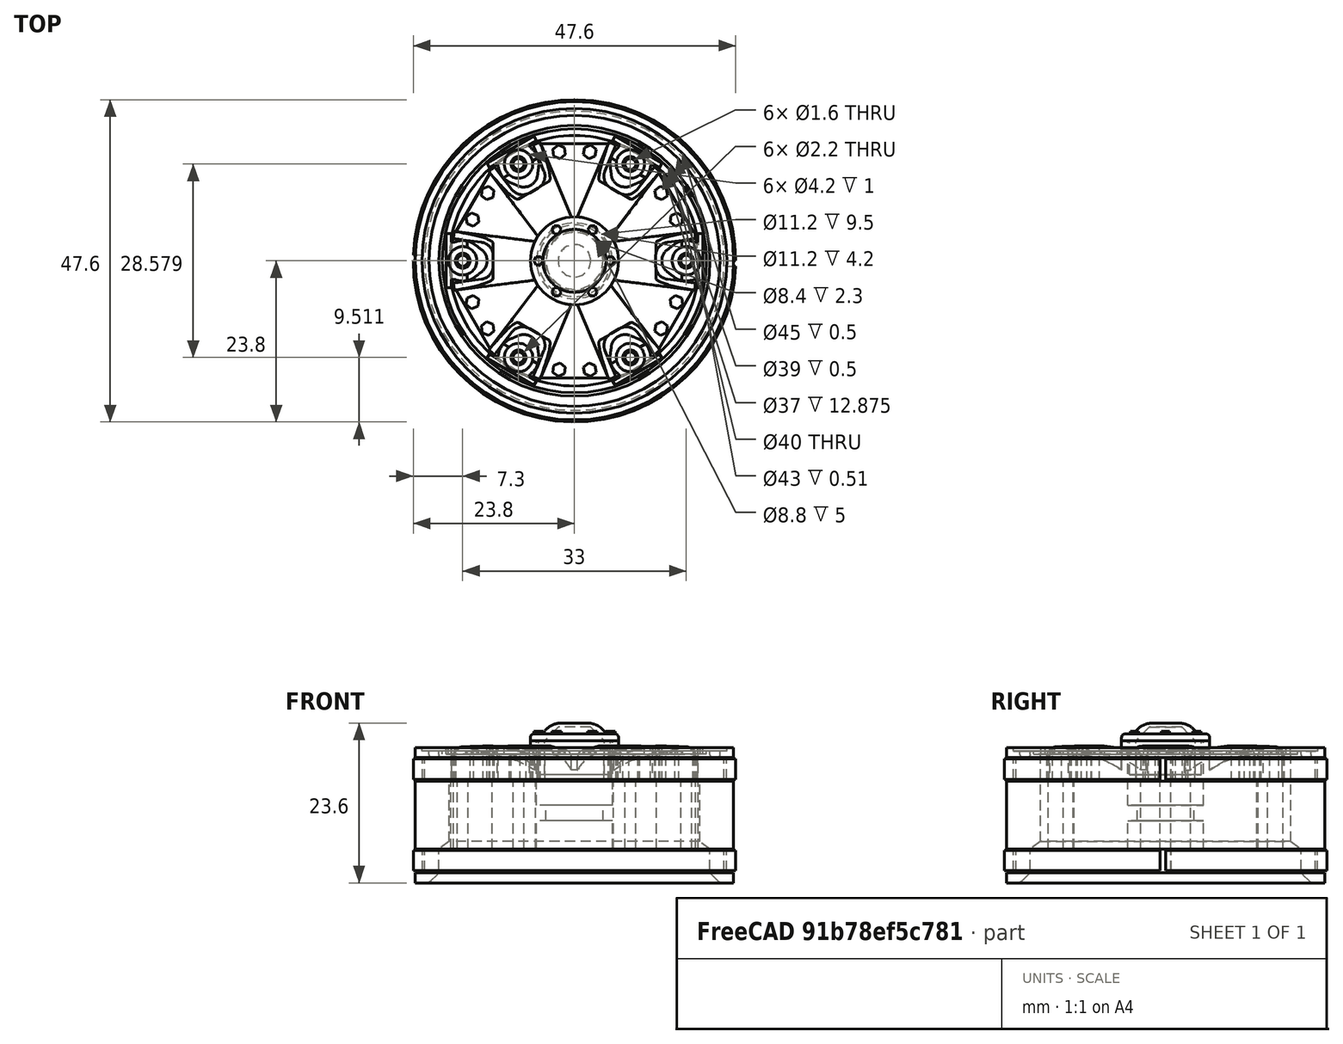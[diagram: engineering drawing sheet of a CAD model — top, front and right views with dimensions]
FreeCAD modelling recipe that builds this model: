
FCSTD DOCUMENT  (FreeCAD 0.18.4R)
Label: trilex_middle
License: All rights reserved
LicenseURL: http://en.wikipedia.org/wiki/All_rights_reserved
objects: Part::Cylinder×39, Part::MultiFuse×27, Part::Cut×26, Part::Feature×23, Part::Fillet×8, Part::Box×6, Part::Chamfer×6, Part::RegularPolygon×4, Part::Extrusion×4, Part::Cone×2
note: 145 computed .brp shape members not serialized (recipe doc carries the construction recipe); baked Part::Feature solids carry a one-line shape summary decoded from their .brp

FEATURE [Part::Cylinder] Cylinder
  Angle = 360
  AttacherType = Attacher::AttachEngine3D
  Height = 20
  Radius = 23.5
FEATURE [Part::RegularPolygon] RegularPolygon001  label="Regular polygon001"
  AttacherType = Attacher::AttachEngine3D
  Circumradius = 1
  Placement = pos=(16.25,0,18.5) rot=(0,0,1;0rad)
  Polygon = 6
FEATURE [Part::Extrusion] Extrude010
  Base = -> RegularPolygon001
  Dir = (0,0,1)
  DirMode = 0
  FaceMakerClass = Part::FaceMakerBullseye
  LengthFwd = 1
  LengthRev = 0
  Placement = pos=(0,0,0) rot=(0,0,1;0.383972rad)
  Solid = true
  Symmetric = false
FEATURE [Part::Feature] Fillet006004001  label="Fillet006008"
  Placement = pos=(0,0,0) rot=(0,0,1;1.0472rad)
  shape: bbox 9.68 x 11.05 x 7 mm, 10 faces (baked)
FEATURE [Part::Feature] Fillet006004005  label="Fillet006012"
  Placement = pos=(0,0,0) rot=(0,0,-1;1.0472rad)
  shape: bbox 9.68 x 11.05 x 7 mm, 10 faces (baked)
FEATURE [Part::Cylinder] Cylinder018
  Angle = 360
  AttacherType = Attacher::AttachEngine3D
  Height = 0.5
  Placement = pos=(0,0,19.5) rot=(0,0,1;0rad)
  Radius = 22.5
FEATURE [Part::Cylinder] Cylinder027
  Angle = 360
  AttacherType = Attacher::AttachEngine3D
  Height = 4
  Placement = pos=(0,0,3) rot=(0,0,1;0rad)
  Radius = 4.2
FEATURE [Part::Cylinder] Cylinder002
  Angle = 360
  AttacherType = Attacher::AttachEngine3D
  Height = 17
  Radius = 22.1
FEATURE [Part::Cylinder] Cylinder007
  Angle = 360
  AttacherType = Attacher::AttachEngine3D
  Height = 1
  Placement = pos=(0,0,19) rot=(0,0,1;0rad)
  Radius = 19.5
FEATURE [Part::Cylinder] Cylinder025
  Angle = 360
  AttacherType = Attacher::AttachEngine3D
  Height = 4.2
  Radius = 5.6
FEATURE [Part::Cylinder] Cylinder003
  Angle = 360
  AttacherType = Attacher::AttachEngine3D
  Height = 17
  Radius = 22
FEATURE [Part::Cylinder] Cylinder026
  Angle = 360
  AttacherType = Attacher::AttachEngine3D
  Height = 10
  Placement = pos=(0,0,6.5) rot=(0,0,1;0rad)
  Radius = 5.6
FEATURE [Part::Cylinder] Cylinder004
  Angle = 360
  AttacherType = Attacher::AttachEngine3D
  Height = 10
  Placement = pos=(0,0,0.5) rot=(0,0,1;0rad)
  Radius = 23.5
FEATURE [Part::Cylinder] Cylinder006
  Angle = 360
  AttacherType = Attacher::AttachEngine3D
  Height = 20
  Radius = 18.5
FEATURE [Part::Cylinder] Cylinder001
  Angle = 360
  AttacherType = Attacher::AttachEngine3D
  Height = 17
  Radius = 23.5
FEATURE [Part::Feature] Cut057003014003  label="Cut057003017"
  Placement = pos=(0,0,0) rot=(0,0,1;3.14159rad)
  shape: bbox 12.98 x 8.687 x 5.868 mm, 9 faces (baked)
FEATURE [Part::Feature] Extrude010001  label="Extrude011"
  Placement = pos=(0,0,0) rot=(0,0,1;0.663225rad)
  shape: bbox 1.854 x 1.981 x 1 mm, 8 faces (baked)
FEATURE [Part::MultiFuse] Fusion058
  Refine = true
  Shapes = -> [Extrude010001,Extrude010]
FEATURE [Part::Feature] Fusion058001  label="Fusion059"
  Placement = pos=(0,0,0) rot=(0,0,1;1.0472rad)
  shape: bbox 6.377 x 1.981 x 1 mm, 16 faces, 2 solids (baked)
FEATURE [Part::Feature] Fusion058005  label="Fusion063"
  Placement = pos=(0,0,0) rot=(0,0,-1;1.0472rad)
  shape: bbox 4.116 x 5.898 x 1 mm, 16 faces, 2 solids (baked)
FEATURE [Part::Feature] Fusion058004  label="Fusion062"
  Placement = pos=(0,0,0) rot=(0,0,1;4.18879rad)
  shape: bbox 6.377 x 1.981 x 1 mm, 16 faces, 2 solids (baked)
FEATURE [Part::Feature] Fillet006004003  label="Fillet006010"
  Placement = pos=(0,0,0) rot=(0,0,1;3.14159rad)
  shape: bbox 10 x 7 x 7 mm, 10 faces (baked)
FEATURE [Part::Feature] Fusion058002  label="Fusion060"
  Placement = pos=(0,0,0) rot=(0,0,1;2.0944rad)
  shape: bbox 4.116 x 5.898 x 1 mm, 16 faces, 2 solids (baked)
FEATURE [Part::Cut] Cut002
  Base = -> Cylinder004
  Placement = pos=(0,0,4.5) rot=(0,0,1;0rad)
  Refine = true
  Tool = -> Cylinder003
FEATURE [Part::Feature] Cut057003014004  label="Cut057003018"
  Placement = pos=(0,0,0) rot=(0,0,1;4.18879rad)
  shape: bbox 12.4 x 14.34 x 5.868 mm, 9 faces (baked)
FEATURE [Part::Cut] Cut
  Base = -> Cylinder001
  Placement = pos=(0,0,1.5) rot=(0,0,1;0rad)
  Refine = true
  Tool = -> Cylinder002
FEATURE [Part::Cut] Cut001
  Base = -> Cylinder
  Refine = true
  Tool = -> Cut
FEATURE [Part::MultiFuse] Fusion
  Refine = true
  Shapes = -> [Cut002,Cut001]
FEATURE [Part::MultiFuse] Fusion006
  Placement = pos=(0,0,5) rot=(0,0,1;0rad)
  Refine = true
  Shapes = -> [Cylinder025,Cylinder026,Cylinder027]
FEATURE [Part::Cylinder] Cylinder101
  Angle = 360
  AttacherType = Attacher::AttachEngine3D
  Height = 3.8
  Placement = pos=(0,0,19.4) rot=(0,0,1;0rad)
  Radius = 5
FEATURE [Part::Cylinder] Cylinder102
  Angle = 288
  AttacherType = Attacher::AttachEngine3D
  Height = 5
  Placement = pos=(16.5,0,15) rot=(0,0,1;0.628319rad)
  Radius = 3
FEATURE [Part::Box] Box012  label="Cube012"
  AttacherType = Attacher::AttachEngine3D
  Height = 5
  Length = 2
  Placement = pos=(16.5,-2.75,15) rot=(0,0,1;0rad)
  Width = 5.5
FEATURE [Part::Cylinder] Cylinder103
  Angle = 360
  AttacherType = Attacher::AttachEngine3D
  Height = 5
  Placement = pos=(15.5,0,15) rot=(0,0,1;0rad)
  Radius = 1.1
FEATURE [Part::Box] Box013  label="Cube013"
  AttacherType = Attacher::AttachEngine3D
  Height = 5
  Length = 0.75
  Placement = pos=(18.2,-4,15) rot=(0,0,1;0rad)
  Width = 8
FEATURE [Part::Cylinder] Cylinder104
  Angle = 360
  AttacherType = Attacher::AttachEngine3D
  Height = 1
  Placement = pos=(15.5,0,19) rot=(0,0,1;0rad)
  Radius = 2.1
FEATURE [Part::MultiFuse] Fusion044
  Refine = true
  Shapes = -> [Box012,Box013,Cylinder102]
FEATURE [Part::MultiFuse] Fusion045
  Placement = pos=(1,0,0) rot=(0,0,1;0rad)
  Refine = true
  Shapes = -> [Cylinder103,Cylinder104]
FEATURE [Part::Box] Box014  label="Cube014"
  AttacherType = Attacher::AttachEngine3D
  Height = 1
  Length = 7
  Placement = pos=(11.2,-4,18.75) rot=(0,-1,0;0.261799rad)
  Width = 8
FEATURE [Part::Cylinder] Cylinder105
  Angle = 360
  AttacherType = Attacher::AttachEngine3D
  Height = 5
  Placement = pos=(15,0,15) rot=(0,0,1;0rad)
  Radius = 2.1
FEATURE [Part::MultiFuse] Fusion046
  Refine = true
  Shapes = -> [Fusion044,Cylinder105]
FEATURE [Part::Feature] Cut057003001  label="Cut057005"
  Placement = pos=(0,0,0) rot=(0,0,1;1.0472rad)
  shape: bbox 7.689 x 7.521 x 5.306 mm, 18 faces (baked)
FEATURE [Part::Feature] Cut057003002  label="Cut057006"
  Placement = pos=(0,0,0) rot=(0,0,1;2.0944rad)
  shape: bbox 7.689 x 7.521 x 5.306 mm, 18 faces (baked)
FEATURE [Part::Feature] Cut057003003  label="Cut057007"
  Placement = pos=(0,0,0) rot=(0,0,1;3.14159rad)
  shape: bbox 6.05 x 8 x 5.306 mm, 18 faces (baked)
FEATURE [Part::Feature] Cut057003004  label="Cut057008"
  Placement = pos=(0,0,0) rot=(0,0,1;4.18879rad)
  shape: bbox 7.689 x 7.521 x 5.306 mm, 18 faces (baked)
FEATURE [Part::Feature] Cut057003005  label="Cut057009"
  Placement = pos=(0,0,0) rot=(0,0,-1;1.0472rad)
  shape: bbox 7.689 x 7.521 x 5.306 mm, 18 faces (baked)
FEATURE [Part::Cylinder] Cylinder126
  Angle = 360
  AttacherType = Attacher::AttachEngine3D
  Height = 2
  Placement = pos=(0,0,19) rot=(0,0,1;0rad)
  Radius = 21.5
FEATURE [Part::Cylinder] Cylinder127
  Angle = 360
  AttacherType = Attacher::AttachEngine3D
  Height = 2
  Placement = pos=(0,0,19) rot=(0,0,1;0rad)
  Radius = 20
FEATURE [Part::Cut] Cut061004
  Base = -> Cylinder126
  Placement = pos=(0,0,-0.5) rot=(0,0,1;0rad)
  Refine = true
  Tool = -> Cylinder127
FEATURE [Part::RegularPolygon] RegularPolygon  label="Regular polygon"
  AttacherType = Attacher::AttachEngine3D
  Circumradius = 20
  Polygon = 6
FEATURE [Part::Cylinder] Cylinder128
  Angle = 360
  AttacherType = Attacher::AttachEngine3D
  Height = 15
  Placement = pos=(0,0,5) rot=(0,0,1;0rad)
  Radius = 18.25
FEATURE [Part::Extrusion] Extrude009
  Base = -> RegularPolygon
  Dir = (0,0,-1)
  DirMode = 0
  FaceMakerClass = Part::FaceMakerBullseye
  LengthFwd = 14
  LengthRev = 0
  Placement = pos=(0,0,19) rot=(0,0,1;0rad)
  Solid = true
  Symmetric = false
FEATURE [Part::Cylinder] Cylinder129
  Angle = 360
  AttacherType = Attacher::AttachEngine3D
  Height = 15
  Placement = pos=(0,0,5) rot=(0,0,1;0rad)
  Radius = 25
FEATURE [Part::Cut] Cut057003007
  Base = -> Cylinder129
  Refine = true
  Tool = -> Cylinder128
FEATURE [Part::Cut] Cut057003008
  Base = -> Extrude009
  Refine = true
  Tool = -> Cut057003007
FEATURE [Part::Cylinder] Cylinder130
  Angle = 360
  AttacherType = Attacher::AttachEngine3D
  Height = 6
  Placement = pos=(0,0,15) rot=(0,0,1;0rad)
  Radius = 6.5
FEATURE [Part::Cylinder] Cylinder131
  Angle = 360
  AttacherType = Attacher::AttachEngine3D
  Height = 15
  Placement = pos=(-16.5,0,1) rot=(0,0,1;0rad)
  Radius = 0.8
FEATURE [Part::Cylinder] Cylinder132
  Angle = 360
  AttacherType = Attacher::AttachEngine3D
  Height = 15
  Placement = pos=(16.5,0,1) rot=(0,0,1;0rad)
  Radius = 0.8
FEATURE [Part::Cylinder] Cylinder133
  Angle = 360
  AttacherType = Attacher::AttachEngine3D
  Height = 15
  Placement = pos=(-16.5,0,1) rot=(0,0,1;0rad)
  Radius = 0.8
FEATURE [Part::MultiFuse] Fusion051
  Placement = pos=(0,0,0) rot=(0,0,1;1.0472rad)
  Refine = true
  Shapes = -> [Cylinder133,Cylinder132]
FEATURE [Part::Cylinder] Cylinder134
  Angle = 360
  AttacherType = Attacher::AttachEngine3D
  Height = 15
  Placement = pos=(-16.5,0,1) rot=(0,0,1;0rad)
  Radius = 0.8
FEATURE [Part::Cylinder] Cylinder135
  Angle = 360
  AttacherType = Attacher::AttachEngine3D
  Height = 15
  Placement = pos=(16.5,0,1) rot=(0,0,1;0rad)
  Radius = 0.8
FEATURE [Part::MultiFuse] Fusion052
  Placement = pos=(0,0,0) rot=(0,0,1;2.0944rad)
  Refine = true
  Shapes = -> [Cylinder134,Cylinder135]
FEATURE [Part::Box] Box015  label="Cube015"
  AttacherType = Attacher::AttachEngine3D
  Height = 6
  Length = 17
  Placement = pos=(5,-4.5,15) rot=(0,0,1;0rad)
  Width = 9
FEATURE [Part::Chamfer] Chamfer004
  Base = -> Box015
  Edges = 2 edges: [Edge1 r1=1.75 r2=14,Edge3 r1=1.75 r2=14]
FEATURE [Part::Chamfer] Chamfer005
  Base = -> Chamfer004
  Edges = 1 edges: [Edge1 r1=1.5 r2=14]
FEATURE [Part::Box] Box  label="Cube"
  AttacherType = Attacher::AttachEngine3D
  Height = 7
  Length = 10
  Placement = pos=(12,-3.5,15) rot=(0,0,1;0rad)
  Width = 7
FEATURE [Part::Chamfer] Chamfer003
  Base = -> Box
  Edges = 2 edges: [Edge1 r1=1 r2=7.5,Edge3 r1=1 r2=7.5]
FEATURE [Part::Fillet] Fillet006004
  Base = -> Chamfer003
  Edges = 2 edges r=2: [Edge2,Edge3]
FEATURE [Part::Feature] Fillet006004002  label="Fillet006009"
  Placement = pos=(0,0,0) rot=(0,0,1;2.0944rad)
  shape: bbox 9.68 x 11.05 x 7 mm, 10 faces (baked)
FEATURE [Part::Feature] Fillet006004004  label="Fillet006011"
  Placement = pos=(0,0,0) rot=(0,0,1;4.18879rad)
  shape: bbox 9.68 x 11.05 x 7 mm, 10 faces (baked)
FEATURE [Part::MultiFuse] Fusion057
  Refine = true
  Shapes = -> [Fillet006004005,Fillet006004001,Fillet006004003,Fillet006004,Fillet006004002,Fillet006004004]
FEATURE [Part::Feature] Cut057003014005  label="Cut057003019"
  Placement = pos=(0,0,0) rot=(0,0,-1;1.0472rad)
  shape: bbox 12.4 x 14.34 x 5.868 mm, 9 faces (baked)
FEATURE [Part::Box] Box016  label="Cube016"
  AttacherType = Attacher::AttachEngine3D
  Height = 6
  Length = 17
  Placement = pos=(5,-4.5,20.5) rot=(0,1,0;0.034907rad)
  Width = 9
FEATURE [Part::Cylinder] Cylinder138
  Angle = 360
  AttacherType = Attacher::AttachEngine3D
  Height = 10
  Placement = pos=(0,0,10) rot=(0,0,1;0rad)
  Radius = 6
FEATURE [Part::Fillet] Fillet006004006
  Base = -> Cylinder101
  Edges = 1 edges r=3: [Edge1]
  Placement = pos=(0,0,0.4) rot=(0,0,1;0rad)
FEATURE [Part::Chamfer] Chamfer
  Base = -> Fusion046
  Edges = 2 edges r=0.85: [Edge25,Edge27]
FEATURE [Part::Cut] Cut057002
  Base = -> Chamfer
  Refine = true
  Tool = -> Fusion045
FEATURE [Part::Cut] Cut057003
  Base = -> Cut057002
  Refine = true
  Tool = -> Box014
FEATURE [Part::MultiFuse] Fusion047
  Refine = true
  Shapes = -> [Cut057003,Cut057003001,Cut057003002,Cut057003003,Cut057003004,Cut057003005]
FEATURE [Part::Cylinder] Cylinder057
  Angle = 360
  AttacherType = Attacher::AttachEngine3D
  Height = 15
  Placement = pos=(16.5,0,1) rot=(0,0,1;0rad)
  Radius = 0.8
FEATURE [Part::MultiFuse] Fusion050
  Refine = true
  Shapes = -> [Cylinder131,Cylinder057]
FEATURE [Part::MultiFuse] Fusion053
  Refine = true
  Shapes = -> [Fusion052,Fusion051,Fusion050]
FEATURE [Part::Cylinder] Cylinder070
  Angle = 360
  AttacherType = Attacher::AttachEngine3D
  Height = 5
  Radius = 20
FEATURE [Part::Cut] Cut031
  Base = -> Fusion
  Refine = true
  Tool = -> Cylinder006
FEATURE [Part::Cut] Cut032
  Base = -> Cut031
  Refine = true
  Tool = -> Cylinder018
FEATURE [Part::Cut] Cut033
  Base = -> Cut032
  Refine = true
  Tool = -> Cylinder007
FEATURE [Part::Cut] Cut034
  Base = -> Cut033
  Refine = true
  Tool = -> Cylinder070
FEATURE [Part::Cylinder] Cylinder078
  Angle = 178
  AttacherType = Attacher::AttachEngine3D
  Height = 3
  Placement = pos=(0,0,1.8) rot=(0,0,1;0rad)
  Radius = 23.8
FEATURE [Part::Cylinder] Cylinder079
  Angle = 360
  AttacherType = Attacher::AttachEngine3D
  Height = 17
  Radius = 22.45
FEATURE [Part::Cut] Cut035
  Base = -> Cylinder078
  Refine = true
  Tool = -> Cylinder079
FEATURE [Part::Cylinder] Cylinder080
  Angle = 178
  AttacherType = Attacher::AttachEngine3D
  Height = 3
  Placement = pos=(0,0,1.8) rot=(0,0,1;0rad)
  Radius = 23.8
FEATURE [Part::Cylinder] Cylinder081
  Angle = 360
  AttacherType = Attacher::AttachEngine3D
  Height = 17
  Radius = 22.45
FEATURE [Part::Cut] Cut036
  Base = -> Cylinder080
  Placement = pos=(0,0,0) rot=(0,0,1;3.14159rad)
  Refine = true
  Tool = -> Cylinder081
FEATURE [Part::MultiFuse] Fusion032
  Placement = pos=(0,0,13.5) rot=(0,0,1;0rad)
  Refine = true
  Shapes = -> [Cut035,Cut036]
FEATURE [Part::Cut] Cut037
  Base = -> Cylinder080
  Placement = pos=(0,0,0) rot=(0,0,1;3.14159rad)
  Refine = true
  Tool = -> Cylinder081
FEATURE [Part::Cut] Cut038
  Base = -> Cylinder078
  Refine = true
  Tool = -> Cylinder079
FEATURE [Part::MultiFuse] Fusion033
  Refine = true
  Shapes = -> [Cut038,Cut037]
FEATURE [Part::MultiFuse] Fusion034  label="trilex-middle-rim-support"
  Refine = true
  Shapes = -> [Fusion032,Fusion033]
FEATURE [Part::Cone] Cone
  Angle = 360
  AttacherType = Attacher::AttachEngine3D
  Height = 6
  Placement = pos=(0,0,5) rot=(0,0,1;0rad)
  Radius1 = 20
  Radius2 = 12
FEATURE [Part::Cut] Cut057004
  Base = -> Cut034
  Refine = true
  Tool = -> Cone
FEATURE [Part::Chamfer] Chamfer002
  Base = -> Cut057004
  Edges = 1 edges r=1.5: [Edge17]
FEATURE [Part::Fillet] Fillet006002
  Base = -> Chamfer002
  Edges = 2 edges r=1: [Edge1,Edge4]
FEATURE [Part::Cut] Cut057003006
  Base = -> Fillet006002
  Refine = true
  Tool = -> Cut061004
FEATURE [Part::Cylinder] Cylinder098
  Angle = 360
  AttacherType = Attacher::AttachEngine3D
  Height = 11
  Placement = pos=(0,0,12) rot=(0,0,1;0rad)
  Radius = 4.4
FEATURE [Part::Cylinder] Cylinder097
  Angle = 360
  AttacherType = Attacher::AttachEngine3D
  Height = 8.6
  Placement = pos=(0,0,11.5) rot=(0,0,1;0rad)
  Radius = 5.3
FEATURE [Part::Cylinder] Cylinder099
  Angle = 360
  AttacherType = Attacher::AttachEngine3D
  Height = 1
  Placement = pos=(0,0,20) rot=(0,0,1;0rad)
  Radius = 6.5
FEATURE [Part::Fillet] Fillet059
  Base = -> Cylinder099
  Edges = 1 edges r=0.5: [Edge1]
FEATURE [Part::Cylinder] Cylinder100
  Angle = 360
  AttacherType = Attacher::AttachEngine3D
  Height = 5
  Placement = pos=(0,0,11) rot=(0,0,1;0rad)
  Radius = 6
FEATURE [Part::MultiFuse] Fusion041
  Refine = true
  Shapes = -> [Cylinder098,Cylinder100]
FEATURE [Part::Chamfer] Chamfer001
  Base = -> Fusion041
  Edges = 1 edges r=2: [Edge1]
FEATURE [Part::Fillet] Fillet006003
  Base = -> Cut057003006
  Edges = 3 edges r=0.49: [Edge34,Edge36,Edge39]
FEATURE [Part::MultiFuse] Fusion048  label="trilex-middle-rim"
  Refine = true
  Shapes = -> [Fillet006003,Cut057003006,Fusion047]
FEATURE [Part::Fillet] Fillet006005
  Base = -> Chamfer005
  Edges = 2 edges r=1: [Edge5,Edge9]
FEATURE [Part::Cylinder] Cylinder137
  Angle = 360
  AttacherType = Attacher::AttachEngine3D
  Height = 10
  Placement = pos=(0,0,5) rot=(0,0,1;0rad)
  Radius = 25
FEATURE [Part::Feature] Fusion058003  label="Fusion061"
  Placement = pos=(0,0,0) rot=(0,0,1;3.14159rad)
  shape: bbox 4.116 x 5.898 x 1 mm, 16 faces, 2 solids (baked)
FEATURE [Part::MultiFuse] Fusion058006
  Refine = true
  Shapes = -> [Fusion058,Fusion058001,Fusion058005,Fusion058004,Fusion058002,Fusion058003]
FEATURE [Part::Cone] Cone001
  Angle = 360
  AttacherType = Attacher::AttachEngine3D
  Height = 3
  Placement = pos=(0,0,16) rot=(0,0,1;0rad)
  Radius1 = 5.5
  Radius2 = 10
FEATURE [Part::Cut] Cut057003014006
  Base = -> Cut057003008
  Refine = true
  Tool = -> Cone001
FEATURE [Part::Fillet] Fillet006006
  Base = -> Cut057003014006
  Edges = 1 edges r=13: [Edge17]
FEATURE [Part::Cylinder] Cylinder136
  Angle = 360
  AttacherType = Attacher::AttachEngine3D
  Height = 10
  Placement = pos=(0,0,5) rot=(0,0,1;0rad)
  Radius = 18.25
FEATURE [Part::Cut] Cut057003012
  Base = -> Cylinder137
  Placement = pos=(0,0,7) rot=(0,0,1;0rad)
  Refine = true
  Tool = -> Cylinder136
FEATURE [Part::MultiFuse] Fusion054
  Refine = true
  Shapes = -> [Cut057003012,Cylinder138]
FEATURE [Part::Cut] Cut057003013
  Base = -> Fillet006005
  Refine = true
  Tool = -> Fusion054
FEATURE [Part::Cut] Cut057003014
  Base = -> Cut057003013
  Refine = true
  Tool = -> Box016
FEATURE [Part::Feature] Cut057003014002  label="Cut057003016"
  Placement = pos=(0,0,0) rot=(0,0,1;2.0944rad)
  shape: bbox 12.4 x 14.34 x 5.868 mm, 9 faces (baked)
FEATURE [Part::Feature] Fusion058011002  label="Fusion058013"
  Placement = pos=(0,0,0) rot=(0,0,1;2.0944rad)
  shape: bbox 6.7 x 10.39 x 0.5 mm, 16 faces, 2 solids (baked)
FEATURE [Part::RegularPolygon] RegularPolygon003  label="Regular polygon003"
  AttacherType = Attacher::AttachEngine3D
  Circumradius = 0.7
  Polygon = 6
FEATURE [Part::MultiFuse] Fusion058008
  Placement = pos=(0,0,1) rot=(0,0,1;0rad)
  Refine = true
  Shapes = -> [Fillet059,Cylinder097]
FEATURE [Part::Extrusion] Extrude010003
  Base = -> RegularPolygon003
  Dir = (0,0,1)
  DirMode = 0
  FaceMakerClass = Part::FaceMakerBullseye
  LengthFwd = 0.5
  LengthRev = 0
  Placement = pos=(-5.3,0,21.9) rot=(0,0,1;0rad)
  Solid = true
  Symmetric = false
FEATURE [Part::MultiFuse] Fusion058010
  Refine = true
  Shapes = -> [Fillet006004006,Fusion058008]
FEATURE [Part::RegularPolygon] RegularPolygon002  label="Regular polygon002"
  AttacherType = Attacher::AttachEngine3D
  Circumradius = 0.7
  Polygon = 6
FEATURE [Part::Extrusion] Extrude010002
  Base = -> RegularPolygon002
  Dir = (0,0,1)
  DirMode = 0
  FaceMakerClass = Part::FaceMakerBullseye
  LengthFwd = 0.5
  LengthRev = 0
  Placement = pos=(5.3,0,21.9) rot=(0,0,1;0rad)
  Solid = true
  Symmetric = false
FEATURE [Part::MultiFuse] Fusion058011
  Refine = true
  Shapes = -> [Extrude010003,Extrude010002]
FEATURE [Part::Cut] Cut057003014010
  Base = -> Fusion058010
  Refine = true
  Tool = -> Chamfer001
FEATURE [Part::Feature] Fusion058011001  label="Fusion058012"
  Placement = pos=(0,0,0) rot=(0,0,1;1.0472rad)
  shape: bbox 6.7 x 10.39 x 0.5 mm, 16 faces, 2 solids (baked)
FEATURE [Part::MultiFuse] Fusion058011003
  Refine = true
  Shapes = -> [Fusion058011002,Fusion058011,Fusion058011001]
FEATURE [Part::MultiFuse] Fusion058011004  label="trilex-middle-hub-cap"
  Refine = true
  Shapes = -> [Cut057003014010,Fusion058011003]
FEATURE [Part::Feature] Cut057003014001  label="Cut057003015"
  Placement = pos=(0,0,0) rot=(0,0,1;1.0472rad)
  shape: bbox 12.4 x 14.34 x 5.868 mm, 9 faces (baked)
FEATURE [Part::MultiFuse] Fusion055
  Refine = true
  Shapes = -> [Cut057003014,Cut057003014003,Cut057003014004,Cut057003014005,Cut057003014002,Cut057003014001]
FEATURE [Part::Fillet] Fillet006007
  Base = -> Fusion055
  Edges = 6 edges r=1.5: [Edge16,Edge40,Edge64,Edge88,Edge112,Edge136]
FEATURE [Part::MultiFuse] Fusion056
  Refine = true
  Shapes = -> [Fillet006006,Fillet006007,Cylinder130]
FEATURE [Part::Cut] Cut057003014007
  Base = -> Fusion056
  Refine = true
  Tool = -> Fusion006
FEATURE [Part::Cut] Cut057003014008
  Base = -> Cut057003014007
  Refine = true
  Tool = -> Fusion057
FEATURE [Part::Cut] Cut057003014009
  Base = -> Cut057003014008
  Refine = true
  Tool = -> Fusion053
FEATURE [Part::MultiFuse] Fusion058007  label="trilex-middle-hub"
  Refine = true
  Shapes = -> [Cut057003014009,Fusion058006]
